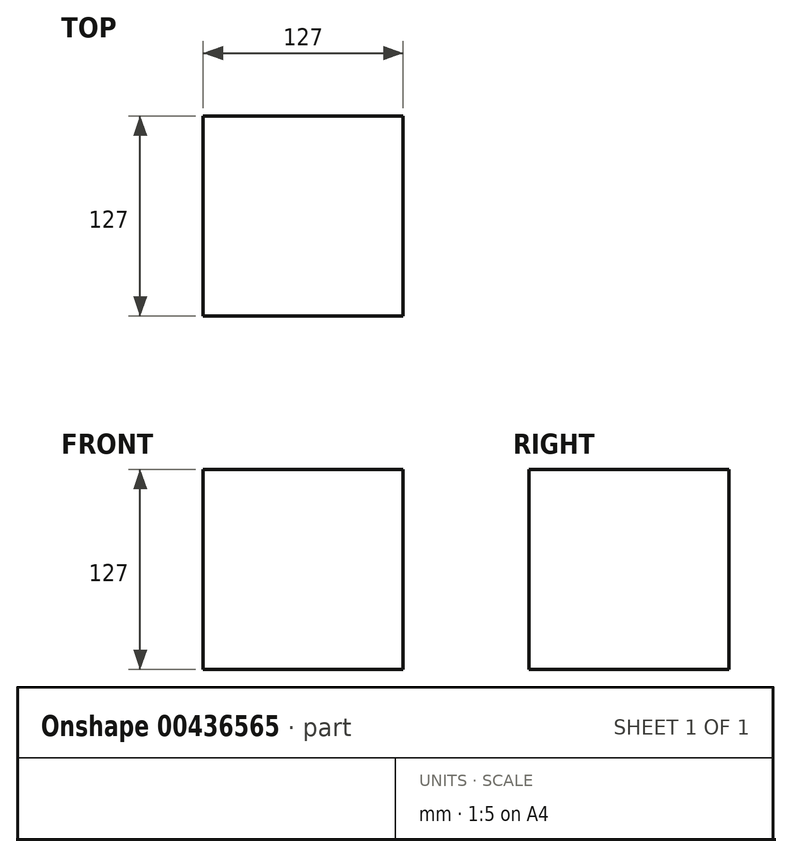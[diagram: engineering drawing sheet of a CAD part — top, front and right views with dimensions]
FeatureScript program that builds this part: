
annotation { "Feature Type Name" : "Feature", "Feature Type Description" : "" }
export const myFeature = defineFeature(function(context is Context, id is Id, definition is map)
    precondition{}
    {
        {
            var Q0;
            Q0=qCreatedBy(makeId("Front.planeOp"),FACE);
            var sketch = newSketch(context, id + "F0", { "sketchPlane" : qUnion([Q0])});
            skLineSegment(sketch, "E0.bottom", {"start": v(-61.47, 63.5) * mm, "end": v(65.53, 63.5) * mm});
            skLineSegment(sketch, "E0.top", {"start": v(-61.47, -63.5) * mm, "end": v(65.53, -63.5) * mm});
            skLineSegment(sketch, "E0.left", {"start": v(-61.47, 63.5) * mm, "end": v(-61.47, -63.5) * mm});
            skLineSegment(sketch, "E0.right", {"start": v(65.53, 63.5) * mm, "end": v(65.53, -63.5) * mm});
            skPoint(sketch, "E0.middle", {"position": v(2.03, 0) * mm});
            skSolve(sketch);
        }
        {
            var Q0;
            Q0=makeQuery(id+"F0.imprint","IMPRINT",FACE,{"disambiguationData":[TD([[makeQuery(id+"F0.imprint","IMPRINT",EDGE,{"derivedFrom":sQuery(id+"F0.wireOp",EDGE,"E0.bottom")}),-1.0]])]});
            extrude(context, id + "F1", {"entities" : qUnion([Q0]), "depth" : 127 * mm});
        }
    });
